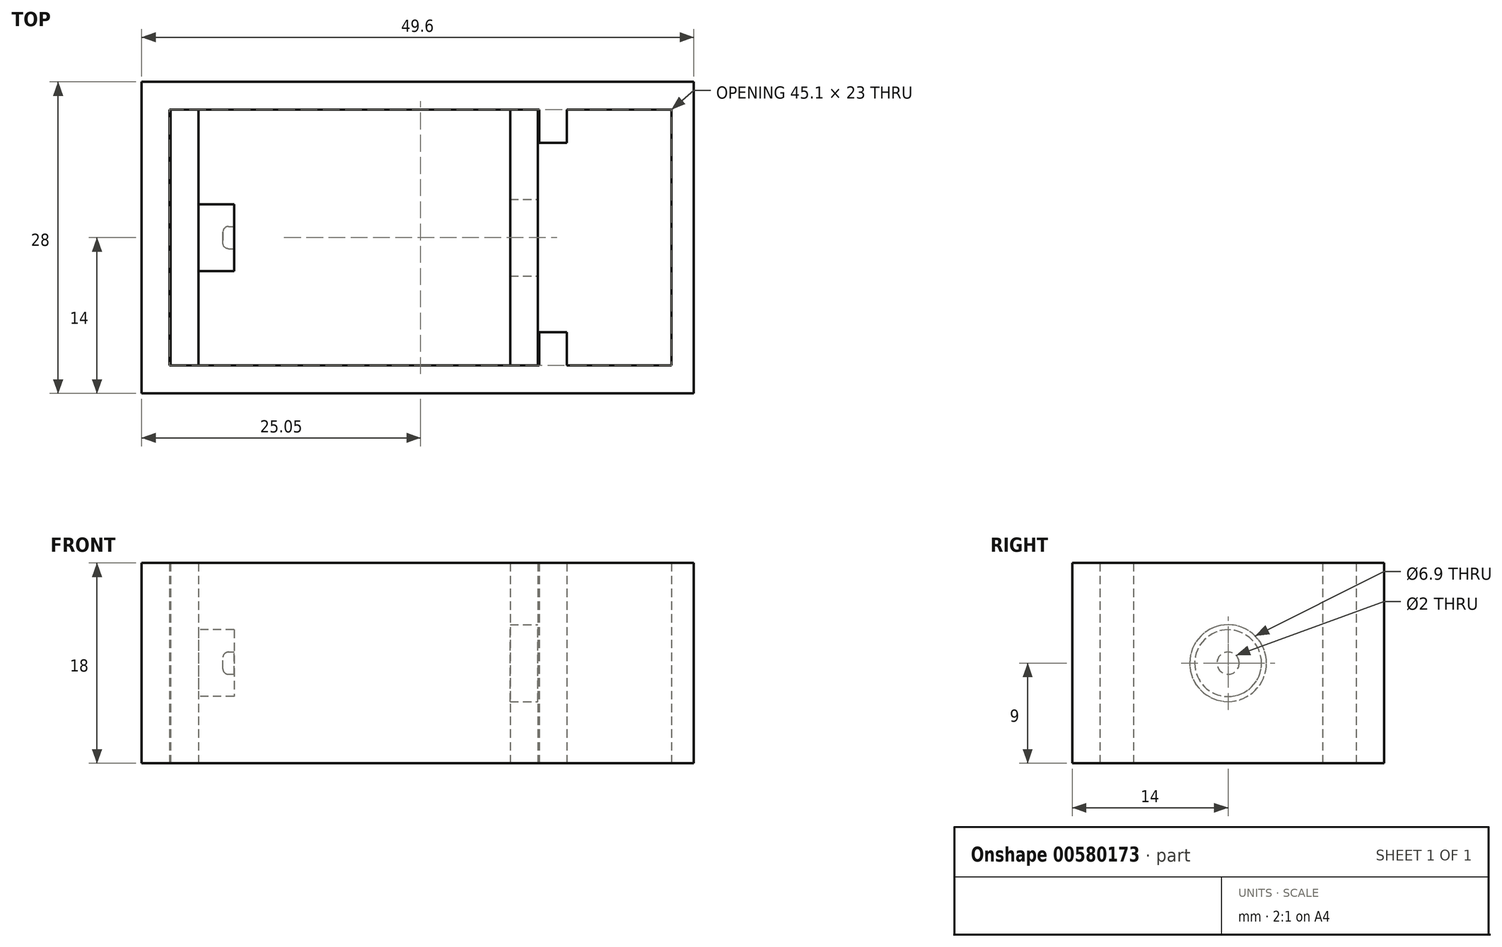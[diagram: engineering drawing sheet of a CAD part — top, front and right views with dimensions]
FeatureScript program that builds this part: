
annotation { "Feature Type Name" : "Feature", "Feature Type Description" : "" }
export const myFeature = defineFeature(function(context is Context, id is Id, definition is map)
    precondition{}
    {
        {
            var Q0;
            Q0=qCreatedBy(makeId("Top.planeOp"),FACE);
            var sketch = newSketch(context, id + "F0", { "sketchPlane" : qUnion([Q0])});
            skLineSegment(sketch, "E0.bottom", {"start": v(14, -9) * mm, "end": v(-14, -9) * mm});
            skLineSegment(sketch, "E0.top", {"start": v(14, 9) * mm, "end": v(-14, 9) * mm});
            skLineSegment(sketch, "E0.left", {"start": v(14, -9) * mm, "end": v(14, 9) * mm});
            skLineSegment(sketch, "E0.right", {"start": v(-14, -9) * mm, "end": v(-14, 9) * mm});
            skPoint(sketch, "E0.middle", {"position": v(0, 0) * mm});
            skLineSegment(sketch, "E1.bottom", {"start": v(16.5, -11.5) * mm, "end": v(-16.5, -11.5) * mm});
            skLineSegment(sketch, "E1.top", {"start": v(16.5, 11.5) * mm, "end": v(-16.5, 11.5) * mm});
            skLineSegment(sketch, "E1.left", {"start": v(16.5, -11.5) * mm, "end": v(16.5, 11.5) * mm});
            skLineSegment(sketch, "E1.right", {"start": v(-16.5, -11.5) * mm, "end": v(-16.5, 11.5) * mm});
            skSolve(sketch);
        }
        {
            var Q0;
            Q0=makeQuery(id+"F0.imprint","IMPRINT",FACE,{"disambiguationData":[TD([[makeQuery(id+"F0.imprint","IMPRINT",EDGE,{"derivedFrom":sQuery(id+"F0.wireOp",EDGE,"E0.bottom")}),1.0]])]});
            extrude(context, id + "F1", {"entities" : qUnion([Q0]), "depth" : 18 * mm, "offsetDistance" : 25 * mm});
        }
        {
            var Q0;
            Q0=makeQuery(id+"F1.opExtrude","SWEPT_FACE",FACE,{"disambiguationData":[OSD([sQuery(id+"F0.wireOp",EDGE,"E1.left")])]});
            var sketch = newSketch(context, id + "F2", { "sketchPlane" : qUnion([Q0])});
            skLineSegment(sketch, "E2", {"start": v(-11.5, 9) * mm, "end": v(11.5, 9) * mm, "construction": true});
            skCircle(sketch, "E3", {"center": v(0, 9) * mm, "radius": 3.45 * mm});
            skSolve(sketch);
        }
        {
            var Q0;
            Q0=makeQuery(id+"F2.imprint","IMPRINT",FACE,{"disambiguationData":[TD([[makeQuery(id+"F2.imprint","IMPRINT",EDGE,{"derivedFrom":sQuery(id+"F2.wireOp",EDGE,"E3")}),1.0]])]});
            extrude(context, id + "F3", {"entities" : qUnion([Q0]), "operationType" : NewBodyOperationType.REMOVE, "oppositeDirection" : true, "depth" : 5 * mm, "offsetDistance" : 25 * mm});
        }
        {
            var Q0;
            Q0=makeQuery(id+"F1.opExtrude","SWEPT_FACE",FACE,{"disambiguationData":[OSD([sQuery(id+"F0.wireOp",EDGE,"E0.right")])]});
            var sketch = newSketch(context, id + "F4", { "sketchPlane" : qUnion([Q0])});
            skCircle(sketch, "E4", {"center": v(0, 9) * mm, "radius": 3 * mm});
            skSolve(sketch);
        }
        {
            var Q0;
            Q0=makeQuery(id+"F4.imprint","IMPRINT",FACE,{"disambiguationData":[TD([[makeQuery(id+"F4.imprint","IMPRINT",EDGE,{"derivedFrom":sQuery(id+"F4.wireOp",EDGE,"E4")}),1.0]])]});
            extrude(context, id + "F5", {"entities" : qUnion([Q0]), "operationType" : NewBodyOperationType.ADD, "depth" : 3.2 * mm, "offsetDistance" : 25 * mm});
        }
        {
            var Q0;
            Q0=makeQuery(id+"F5.opExtrude","CAP_FACE",FACE,{"disambiguationData":[OSD([sQuery(id+"F4.wireOp",EDGE,"E4")])],"isStart":false});
            var sketch = newSketch(context, id + "F6", { "sketchPlane" : qUnion([Q0])});
            skCircle(sketch, "E5", {"center": v(0, 9) * mm, "radius": 1 * mm});
            skSolve(sketch);
        }
        {
            var Q0;
            Q0=makeQuery(id+"F6.imprint","IMPRINT",FACE,{"disambiguationData":[TD([[makeQuery(id+"F6.imprint","IMPRINT",EDGE,{"derivedFrom":sQuery(id+"F6.wireOp",EDGE,"E5")}),1.0]])]});
            extrude(context, id + "F7", {"entities" : qUnion([Q0]), "operationType" : NewBodyOperationType.REMOVE, "oppositeDirection" : true, "depth" : 1 * mm, "offsetDistance" : 25 * mm});
        }
        {
            var Q0;
            Q0=makeQuery(id+"F7.boolean.opBoolean","COPY",EDGE,{"derivedFrom":makeQuery(id+"F7.opExtrude","CAP_EDGE",EDGE,{"disambiguationData":[OSD([sQuery(id+"F6.wireOp",EDGE,"E5")])],"isStart":false})});
            var Q1;
            Q1=makeQuery(id+"F7.boolean.opBoolean","COPY",EDGE,{"derivedFrom":makeQuery(id+"F7.opExtrude","CAP_EDGE",EDGE,{"disambiguationData":[OSD([sQuery(id+"F6.wireOp",EDGE,"E5")])],"isStart":true})});
            fillet(context, id + "F8", {"entities" : qUnion([Q0, Q1]), "tangentPropagation" : true, "radius" : 0.5 * mm, "defaultsChanged" : true, "vertexSettings" : [], "allowEdgeOverflow" : false});
        }
        {
            var Q0;
            Q0=qCreatedBy(makeId("Top.planeOp"),FACE);
            var sketch = newSketch(context, id + "F9", { "sketchPlane" : qUnion([Q0])});
            skLineSegment(sketch, "E6", {"start": v(-16.6, 0) * mm, "end": v(-19.1, 0) * mm});
            skLineSegment(sketch, "E7", {"start": v(-19.1, 0) * mm, "end": v(-19.1, 14) * mm});
            skLineSegment(sketch, "E8", {"start": v(-19.1, 14) * mm, "end": v(30.5, 14) * mm});
            skLineSegment(sketch, "E9", {"start": v(30.5, 14) * mm, "end": v(30.5, 0) * mm});
            skLineSegment(sketch, "E10", {"start": v(30.5, 0) * mm, "end": v(28.5, 0) * mm});
            skLineSegment(sketch, "E11", {"start": v(28.5, 0) * mm, "end": v(28.5, 11.5) * mm});
            skLineSegment(sketch, "E12", {"start": v(28.5, 11.5) * mm, "end": v(13.9, 11.5) * mm});
            skLineSegment(sketch, "E13", {"start": v(13.9, 11.5) * mm, "end": v(13.9, 8.5) * mm});
            skLineSegment(sketch, "E14", {"start": v(13.9, 8.5) * mm, "end": v(11.4, 8.5) * mm});
            skLineSegment(sketch, "E15", {"start": v(11.4, 8.5) * mm, "end": v(11.4, 11.5) * mm});
            skLineSegment(sketch, "E16", {"start": v(11.4, 11.5) * mm, "end": v(-11.4, 11.5) * mm});
            skLineSegment(sketch, "E17", {"start": v(-11.4, 11.5) * mm, "end": v(-11.4, 8.5) * mm});
            skLineSegment(sketch, "E18", {"start": v(-11.4, 8.5) * mm, "end": v(-13.9, 8.5) * mm});
            skLineSegment(sketch, "E19", {"start": v(-13.9, 8.5) * mm, "end": v(-13.9, 11.5) * mm});
            skLineSegment(sketch, "E20", {"start": v(-13.9, 11.5) * mm, "end": v(-16.6, 11.5) * mm});
            skLineSegment(sketch, "E21", {"start": v(-16.6, 11.5) * mm, "end": v(-16.6, 0) * mm});
            skLineSegment(sketch, "E22.MirrorCS", {"start": v(28.5, 0) * mm, "end": v(28.5, -11.5) * mm});
            skLineSegment(sketch, "E23.MirrorCS", {"start": v(-11.4, -8.5) * mm, "end": v(-13.9, -8.5) * mm});
            skLineSegment(sketch, "E24.MirrorCS", {"start": v(13.9, -11.5) * mm, "end": v(13.9, -8.5) * mm});
            skLineSegment(sketch, "E25.MirrorCS", {"start": v(11.4, -11.5) * mm, "end": v(-11.4, -11.5) * mm});
            skLineSegment(sketch, "E26.MirrorCS", {"start": v(-13.9, -11.5) * mm, "end": v(-16.6, -11.5) * mm});
            skLineSegment(sketch, "E27.MirrorCS", {"start": v(-16.6, -11.5) * mm, "end": v(-16.6, 0) * mm});
            skLineSegment(sketch, "E28.MirrorCS", {"start": v(-19.1, 0) * mm, "end": v(-19.1, -14) * mm});
            skLineSegment(sketch, "E29.MirrorCS", {"start": v(28.5, -11.5) * mm, "end": v(13.9, -11.5) * mm});
            skLineSegment(sketch, "E30.MirrorCS", {"start": v(-13.9, -8.5) * mm, "end": v(-13.9, -11.5) * mm});
            skLineSegment(sketch, "E31.MirrorCS", {"start": v(30.5, -14) * mm, "end": v(30.5, 0) * mm});
            skLineSegment(sketch, "E32.MirrorCS", {"start": v(13.9, -8.5) * mm, "end": v(11.4, -8.5) * mm});
            skLineSegment(sketch, "E33.MirrorCS", {"start": v(-11.4, -11.5) * mm, "end": v(-11.4, -8.5) * mm});
            skLineSegment(sketch, "E34.MirrorCS", {"start": v(11.4, -8.5) * mm, "end": v(11.4, -11.5) * mm});
            skLineSegment(sketch, "E35.MirrorCS", {"start": v(-19.1, -14) * mm, "end": v(30.5, -14) * mm});
            skLineSegment(sketch, "E36.bottom", {"start": v(16.6, 11.5) * mm, "end": v(19.1, 11.5) * mm});
            skLineSegment(sketch, "E36.top", {"start": v(16.6, 8.5) * mm, "end": v(19.1, 8.5) * mm});
            skLineSegment(sketch, "E36.left", {"start": v(16.6, 11.5) * mm, "end": v(16.6, 8.5) * mm});
            skLineSegment(sketch, "E36.right", {"start": v(19.1, 11.5) * mm, "end": v(19.1, 8.5) * mm});
            skLineSegment(sketch, "E37.MirrorCS", {"start": v(16.6, -8.5) * mm, "end": v(19.1, -8.5) * mm});
            skLineSegment(sketch, "E38.MirrorCS", {"start": v(19.1, -11.5) * mm, "end": v(19.1, -8.5) * mm});
            skLineSegment(sketch, "E39.MirrorCS", {"start": v(16.6, -11.5) * mm, "end": v(16.6, -8.5) * mm});
            skLineSegment(sketch, "E40.MirrorCS", {"start": v(16.6, -11.5) * mm, "end": v(19.1, -11.5) * mm});
            skSolve(sketch);
        }
        {
            var Q0;
            Q0=makeQuery(id+"F9.imprint","IMPRINT",FACE,{"disambiguationData":[TD([[makeQuery(id+"F9.imprint","IMPRINT",EDGE,{"derivedFrom":sQuery(id+"F9.wireOp",EDGE,"E6")}),-1.0]])]});
            var Q1;
            Q1=makeQuery(id+"F9.imprint","IMPRINT",FACE,{"disambiguationData":[TD([[makeQuery(id+"F9.imprint","IMPRINT",EDGE,{"derivedFrom":sQuery(id+"F9.wireOp",EDGE,"E6")}),1.0]])]});
            var Q2;
            Q2=makeQuery(id+"F9.imprint","IMPRINT",FACE,{"disambiguationData":[TD([[makeQuery(id+"F9.imprint","IMPRINT",EDGE,{"derivedFrom":sQuery(id+"F9.wireOp",EDGE,"E36.top")}),1.0]])]});
            var Q3;
            Q3=makeQuery(id+"F9.imprint","IMPRINT",FACE,{"disambiguationData":[TD([[makeQuery(id+"F9.imprint","IMPRINT",EDGE,{"derivedFrom":sQuery(id+"F9.wireOp",EDGE,"E37.MirrorCS")}),-1.0]])]});
            extrude(context, id + "F10", {"entities" : qUnion([Q0, Q1, Q2, Q3]), "depth" : 18 * mm, "offsetDistance" : 25 * mm});
        }
        {
            var Q0;
            Q0=makeQuery(id+"F1.opExtrude","CAP_FACE",FACE,{"disambiguationData":[OSD([sQuery(id+"F0.wireOp",EDGE,"E0.bottom"),sQuery(id+"F0.wireOp",EDGE,"E0.top"),sQuery(id+"F0.wireOp",EDGE,"E0.left"),sQuery(id+"F0.wireOp",EDGE,"E0.right"),sQuery(id+"F0.wireOp",EDGE,"E1.bottom"),sQuery(id+"F0.wireOp",EDGE,"E1.top"),sQuery(id+"F0.wireOp",EDGE,"E1.left"),sQuery(id+"F0.wireOp",EDGE,"E1.right")])],"isStart":true});
            var sketch = newSketch(context, id + "F11", { "sketchPlane" : qUnion([Q0])});
            skLineSegment(sketch, "E41.bottom", {"start": v(14, -11.5) * mm, "end": v(-14, -11.5) * mm});
            skLineSegment(sketch, "E41.top", {"start": v(14, 11.5) * mm, "end": v(-14, 11.5) * mm});
            skLineSegment(sketch, "E41.left", {"start": v(14, -11.5) * mm, "end": v(14, 11.5) * mm});
            skLineSegment(sketch, "E41.right", {"start": v(-14, -11.5) * mm, "end": v(-14, 11.5) * mm});
            skLineSegment(sketch, "E42.bottom", {"start": v(-14, -4.25) * mm, "end": v(-9.78, -4.25) * mm});
            skLineSegment(sketch, "E42.top", {"start": v(-14, 4.63) * mm, "end": v(-9.78, 4.63) * mm});
            skLineSegment(sketch, "E42.left", {"start": v(-14, -4.25) * mm, "end": v(-14, 4.63) * mm});
            skLineSegment(sketch, "E42.right", {"start": v(-9.78, -4.25) * mm, "end": v(-9.78, 4.63) * mm});
            skSolve(sketch);
        }
        {
            var Q0;
            {var subQ0=sQuery(id+"F11.wireOp",EDGE,"E41.bottom");Q0=makeQuery(id+"F11.imprint","IMPRINT",FACE,{"disambiguationData":[TD([[makeQuery(id+"F11.imprint","IMPRINT",EDGE,{"derivedFrom":subQ0}),-1.0]])]});}
            var Q1;
            {var subQ0=sQuery(id+"F11.wireOp",EDGE,"E41.top");Q1=makeQuery(id+"F11.imprint","IMPRINT",FACE,{"disambiguationData":[TD([[makeQuery(id+"F11.imprint","IMPRINT",EDGE,{"derivedFrom":subQ0}),1.0]])]});}
            var Q2;
            {var subQ2=sQuery(id+"F11.wireOp",EDGE,"E42.bottom");Q2=makeQuery(id+"F11.imprint","IMPRINT",FACE,{"disambiguationData":[TD([[makeQuery(id+"F11.imprint","IMPRINT",EDGE,{"derivedFrom":subQ2}),-1.0]])]});}
            extrude(context, id + "F12", {"entities" : qUnion([Q0, Q1, Q2]), "operationType" : NewBodyOperationType.REMOVE, "oppositeDirection" : true, "depth" : 25 * mm, "offsetDistance" : 25 * mm});
        }
    });
